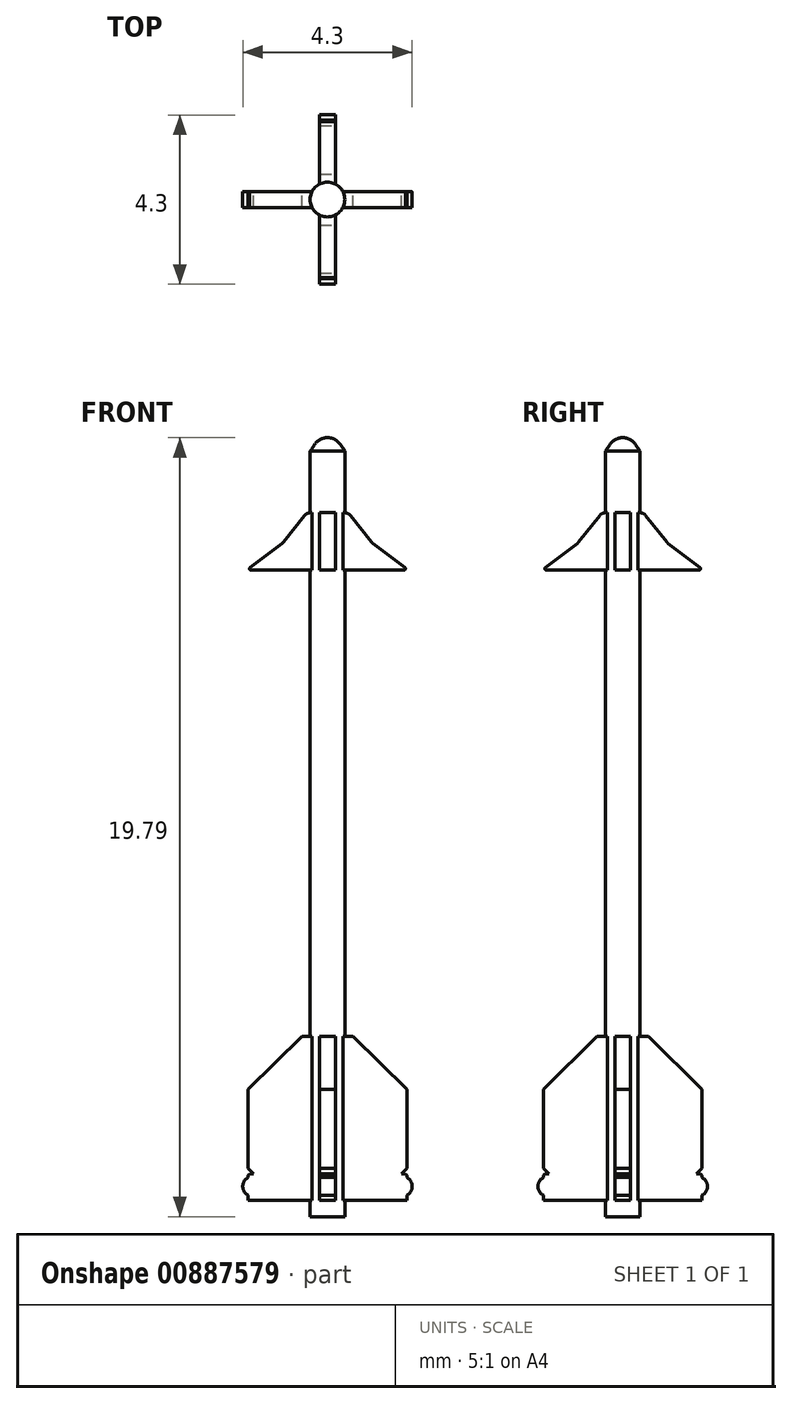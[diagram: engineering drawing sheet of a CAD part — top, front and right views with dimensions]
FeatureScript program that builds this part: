
annotation { "Feature Type Name" : "Feature", "Feature Type Description" : "" }
export const myFeature = defineFeature(function(context is Context, id is Id, definition is map)
    precondition{}
    {
        {
            var Q0;
            Q0=qCreatedBy(makeId("Front.planeOp"),FACE);
            var sketch = newSketch(context, id + "F0", { "sketchPlane" : qUnion([Q0])});
            skLineSegment(sketch, "E0", {"start": v(0, 0) * mm, "end": v(0, 19.8) * mm});
            skLineSegment(sketch, "E1", {"start": v(0.44, 19.44) * mm, "end": v(0.44, 0) * mm});
            skLineSegment(sketch, "E2", {"start": v(0.44, 0) * mm, "end": v(0, 0) * mm});
            skLineSegment(sketch, "E3", {"start": v(0, 19.8) * mm, "end": v(1.85, 19.8) * mm, "construction": true});
            skLineSegment(sketch, "E4", {"start": v(0.44, 19.44) * mm, "end": v(0.32, 19.62) * mm});
            skArc(sketch, "E5", {"start": v(0.32, 19.62) * mm, "mid": v(0.18, 19.75) * mm, "end": v(0, 19.8) * mm});
            skSolve(sketch);
        }
        {
            var Q0;
            Q0=qSketchRegion(id+"F0",true);
            var Q1;
            Q1=sQuery(id+"F0.wireOp",EDGE,"E0");
            revolve(context, id + "F1", {"surfaceOperationType" : NewSurfaceOperationType.NEW, "entities" : qUnion([Q0]), "axis" : qUnion([Q1]), "revolveType" : RevolveType.FULL});
        }
        {
            var Q0;
            Q0=qCreatedBy(makeId("Front.planeOp"),FACE);
            var sketch = newSketch(context, id + "F2", { "sketchPlane" : qUnion([Q0])});
            skLineSegment(sketch, "E6", {"start": v(0.65, 4.58) * mm, "end": v(-0.65, 4.58) * mm});
            skLineSegment(sketch, "E7", {"start": v(-2.01, 3.23) * mm, "end": v(-0.65, 4.58) * mm});
            skLineSegment(sketch, "E8", {"start": v(-2.01, 3.23) * mm, "end": v(-2.01, 1.23) * mm});
            skLineSegment(sketch, "E9", {"start": v(2.01, 1.23) * mm, "end": v(2.01, 3.23) * mm});
            skLineSegment(sketch, "E10", {"start": v(0.65, 4.58) * mm, "end": v(2.01, 3.23) * mm});
            skLineSegment(sketch, "E11", {"start": v(0, 0) * mm, "end": v(0, 4.58) * mm, "construction": true});
            skLineSegment(sketch, "E12", {"start": v(-0.44, 0.8) * mm, "end": v(-0.44, 4.16) * mm, "construction": true});
            skLineSegment(sketch, "E13.0", {"start": v(0.44, 19.44) * mm, "end": v(-0.44, 19.44) * mm});
            skLineSegment(sketch, "E14", {"start": v(-2.01, 0.42) * mm, "end": v(-2.01, 0.54) * mm});
            skLineSegment(sketch, "E15", {"start": v(2.01, 0.42) * mm, "end": v(2.01, 0.54) * mm});
            skLineSegment(sketch, "E16", {"start": v(2.01, 1.23) * mm, "end": v(1.88, 1.1) * mm});
            skLineSegment(sketch, "E17", {"start": v(2.01, 1.05) * mm, "end": v(2.01, 1) * mm});
            skLineSegment(sketch, "E18", {"start": v(-2.01, 1.23) * mm, "end": v(-1.88, 1.1) * mm});
            skLineSegment(sketch, "E19", {"start": v(-2.01, 1.05) * mm, "end": v(-2.01, 1) * mm});
            skArc(sketch, "E20", {"start": v(-2.01, 1) * mm, "mid": v(-2.15, 0.77) * mm, "end": v(-2.01, 0.54) * mm});
            skArc(sketch, "E21", {"start": v(2.01, 0.54) * mm, "mid": v(2.15, 0.77) * mm, "end": v(2.01, 1) * mm});
            skLineSegment(sketch, "E22", {"start": v(-2.01, 1.05) * mm, "end": v(-1.97, 1.1) * mm});
            skLineSegment(sketch, "E23", {"start": v(-1.97, 1.1) * mm, "end": v(-1.88, 1.1) * mm});
            skLineSegment(sketch, "E24", {"start": v(2.01, 1.05) * mm, "end": v(1.97, 1.1) * mm});
            skLineSegment(sketch, "E25", {"start": v(1.97, 1.1) * mm, "end": v(1.88, 1.1) * mm});
            skLineSegment(sketch, "E26", {"start": v(-2.01, 0.42) * mm, "end": v(2.01, 0.42) * mm});
            skLineSegment(sketch, "E27", {"start": v(0, 0) * mm, "end": v(0, 0.42) * mm, "construction": true});
            skLineSegment(sketch, "E28.0", {"start": v(0.44, 0) * mm, "end": v(-0.44, 0) * mm});
            skLineSegment(sketch, "E29", {"start": v(-0.44, 17.88) * mm, "end": v(0.44, 17.88) * mm});
            skArc(sketch, "E30", {"start": v(-0.44, 17.88) * mm, "mid": v(-0.52, 17.86) * mm, "end": v(-0.58, 17.82) * mm});
            skArc(sketch, "E31", {"start": v(0.58, 17.82) * mm, "mid": v(0.52, 17.86) * mm, "end": v(0.44, 17.88) * mm});
            skLineSegment(sketch, "E32", {"start": v(-0.58, 17.82) * mm, "end": v(-1.14, 17.12) * mm});
            skLineSegment(sketch, "E33", {"start": v(-1.14, 17.12) * mm, "end": v(-1.96, 16.5) * mm});
            skLineSegment(sketch, "E34", {"start": v(1.96, 16.5) * mm, "end": v(1.14, 17.12) * mm});
            skLineSegment(sketch, "E35", {"start": v(1.14, 17.12) * mm, "end": v(0.58, 17.82) * mm});
            skLineSegment(sketch, "E36", {"start": v(-1.94, 16.42) * mm, "end": v(1.94, 16.42) * mm});
            skPoint(sketch, "E37.visualSharp", {"position": v(-2.06, 16.42) * mm});
            skArc(sketch, "E37.filletArc", {"start": v(-1.96, 16.5) * mm, "mid": v(-1.98, 16.45) * mm, "end": v(-1.94, 16.42) * mm});
            skPoint(sketch, "E38.visualSharp", {"position": v(2.06, 16.42) * mm});
            skArc(sketch, "E38.filletArc", {"start": v(1.94, 16.42) * mm, "mid": v(1.98, 16.45) * mm, "end": v(1.96, 16.5) * mm});
            skSolve(sketch);
        }
        {
            var Q0;
            Q0=qSketchRegion(id+"F2",true);
            extrude(context, id + "F3", {"entities" : qUnion([Q0]), "operationType" : NewBodyOperationType.ADD, "depth" : .4 * mm, "offsetDistance" : 25 * mm, "symmetric" : true});
        }
        {
            var Q0;
            Q0=makeQuery(id+"F3.opExtrude","SWEPT_EDGE",EDGE,{"disambiguationData":[OSD([sQuery(id+"F2.wireOp",EDGE,"E33"),sQuery(id+"F2.wireOp",EDGE,"E36")])]});
            var Q1;
            Q1=makeQuery(id+"F3.opExtrude","SWEPT_EDGE",EDGE,{"disambiguationData":[OSD([sQuery(id+"F2.wireOp",EDGE,"E34"),sQuery(id+"F2.wireOp",EDGE,"E36")])]});
            fillet(context, id + "F4", {"entities" : qUnion([Q0, Q1]), "radius" : .2 * mm, "tangentPropagation" : true, "allowEdgeOverflow" : false});
        }
        {
            var Q0;
            Q0=makeQuery(id+"F1.opRevolve","SWEPT_BODY",BODY,{"disambiguationData":[OSD([sQuery(id+"F0.wireOp",EDGE,"E0"),sQuery(id+"F0.wireOp",EDGE,"E1"),sQuery(id+"F0.wireOp",EDGE,"E2"),sQuery(id+"F0.wireOp",EDGE,"m1K1lCZm-MTc8-Btmt-IA6e-LtdyprMEJuD3")])]});
            var Q1;
            Q1=makeQuery(id+"F1.opRevolve","SWEPT_FACE",FACE,{"disambiguationData":[OSD([sQuery(id+"F0.wireOp",EDGE,"E1")])]});
            circularPattern(context, id + "F5", {"operationType" : NewBodyOperationType.ADD, "entities" : qUnion([Q0]), "axis" : qUnion([Q1]), "angle" : 360 * degree, "instanceCount" : 4, "equalSpace" : true, "computeTransformsWithoutBuiltin" : true});
        }
    });
